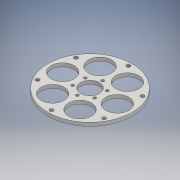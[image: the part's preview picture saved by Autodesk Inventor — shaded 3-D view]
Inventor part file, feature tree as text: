
AUTODESK INVENTOR PART (.ipt)
format: ipt  version: 2019.3 (Build 233278000, 278)  size: 154,112 bytes
history: native  units: mm
features: hole x2, other x1, sketch x1, extrude x1
ambient origin geometry x8: Origin, YZ Plane, XZ Plane, XY Plane, X Axis, Y Axis, Z Axis, Center Point
bodies: Body1 (feature_tree)
feature tree (5):
  other  "SprocketHubPlate"
  sketch  "Sketch1"  dims[d0=66.675mm d1=60.0mm d3=360.0deg d9=33.0mm d19=40.0mm d20=22.0mm d21=60.0mm d23=360.0deg d25=146.0mm d26=60.0mm d28=360.0deg d30=6.0mm d31=0.0mm d32=6.5mm d33=6.0mm d34=4.0mm d35=2.0mm d36=90.0deg d37=8.0mm d38=20.594885mm d39=5.0mm d40=6.0mm d41=4.0mm d42=2.0mm d43=90.0deg d44=8.0mm d45=20.594885mm d46=62.0mm d12=1.0mm d13=1.0mm]
  extrude  "Extrusion2"  Depth=6.0mm TaperAngle=360.0deg
  hole  "Hole2"  [1 undecoded]
  hole  "Hole3"  [1 undecoded]
note: 2 required parameter values undecoded (feature->parameter linkage not recoverable at this tier; creation-order binding heuristic only, values carry confidence <= 0.55)
